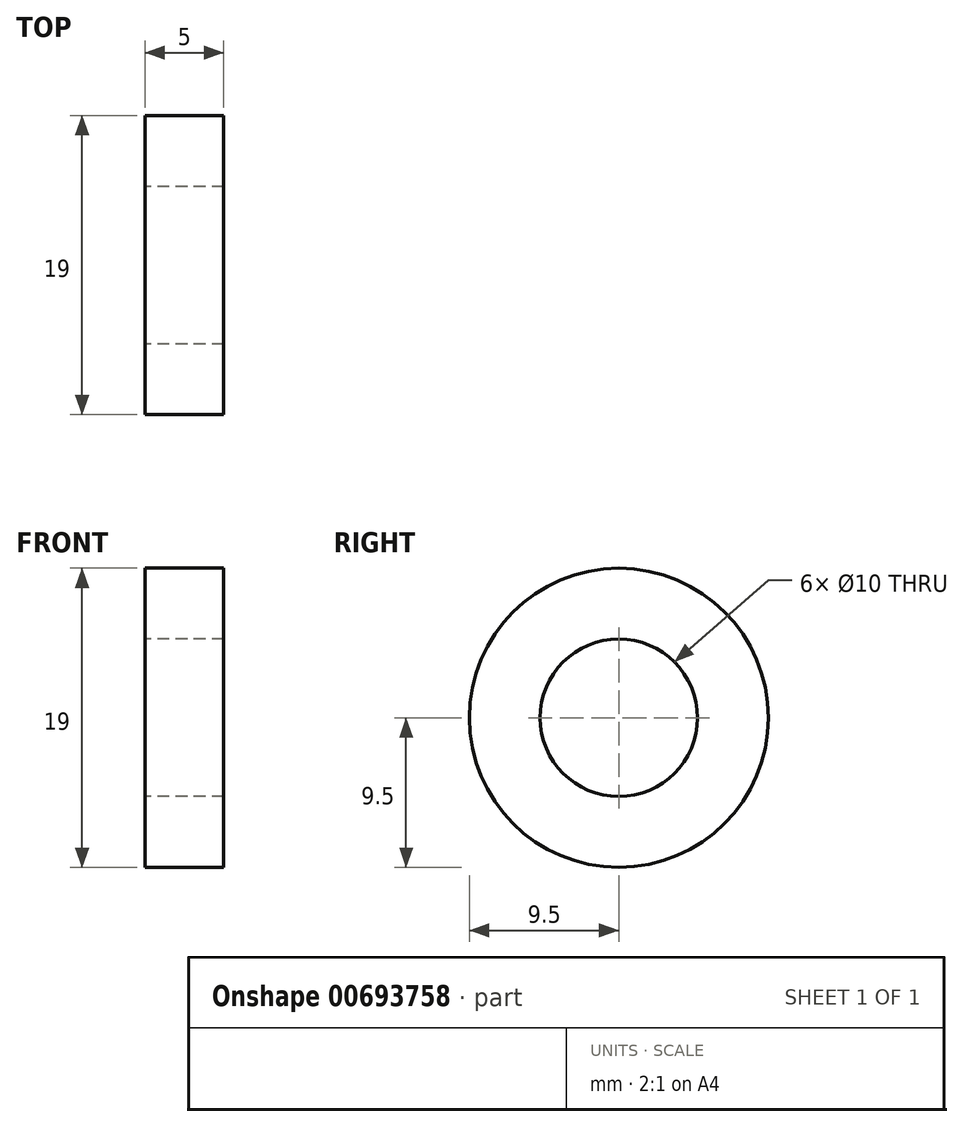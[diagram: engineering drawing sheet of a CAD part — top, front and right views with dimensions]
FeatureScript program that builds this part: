
annotation { "Feature Type Name" : "Feature", "Feature Type Description" : "" }
export const myFeature = defineFeature(function(context is Context, id is Id, definition is map)
    precondition{}
    {
        {
            var Q0;
            Q0=qCreatedBy(makeId("Right.planeOp"),FACE);
            var sketch = newSketch(context, id + "F0", { "sketchPlane" : qUnion([Q0])});
            skCircle(sketch, "E0", {"center": v(0, 0) * mm, "radius": 9.5 * mm});
            skCircle(sketch, "E1", {"center": v(0, 0) * mm, "radius": 5 * mm});
            skSolve(sketch);
        }
        {
            var Q0;
            Q0 = qSketchRegion(id + "F0", true);
            extrude(context, id + "F1", {"entities" : qUnion([Q0]), "depth" : 5 * mm, "offsetDistance" : 25 * mm});
        }
    });
